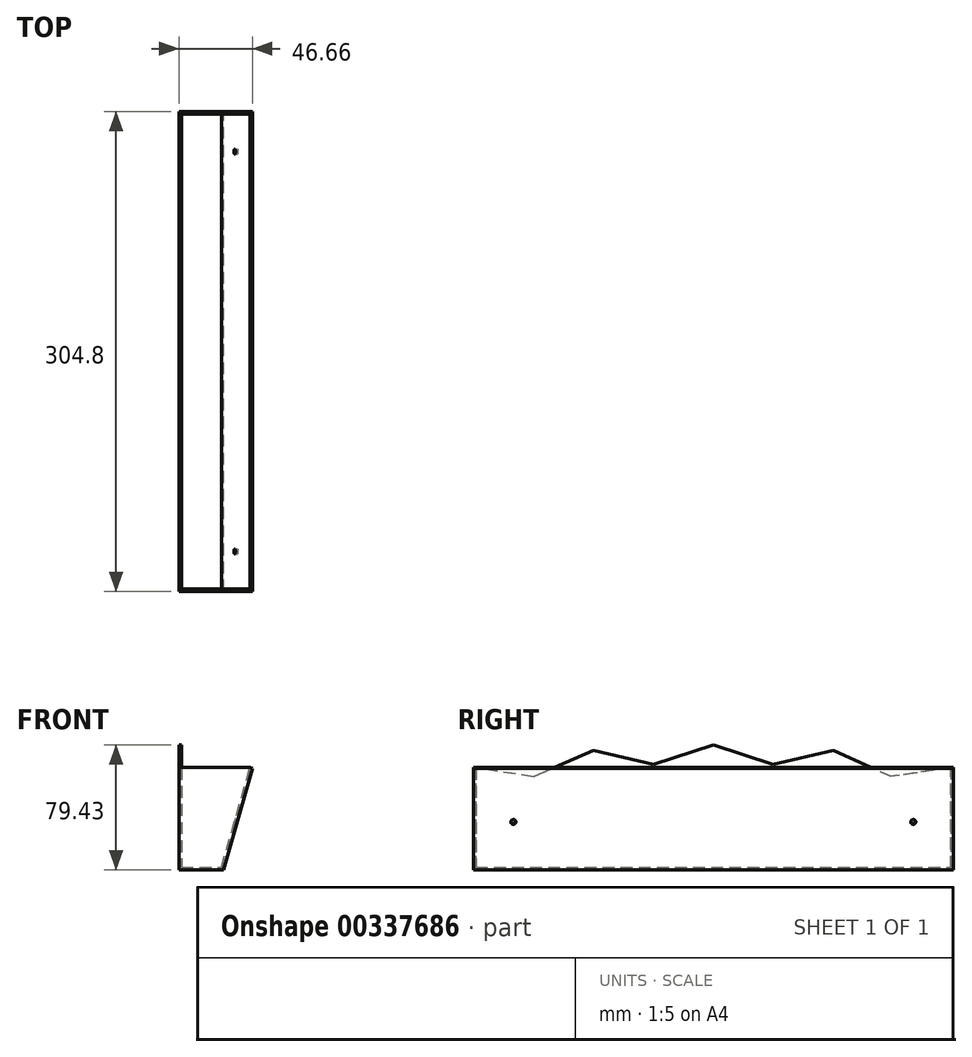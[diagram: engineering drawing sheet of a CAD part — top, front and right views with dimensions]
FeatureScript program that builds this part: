
annotation { "Feature Type Name" : "Feature", "Feature Type Description" : "" }
export const myFeature = defineFeature(function(context is Context, id is Id, definition is map)
    precondition{}
    {
        {
            var Q0;
            Q0=qCreatedBy(makeId("Front.planeOp"),FACE);
            var sketch = newSketch(context, id + "F0", { "sketchPlane" : qUnion([Q0])});
            skLineSegment(sketch, "E0", {"start": v(0, 63.5) * mm, "end": v(0, 0) * mm});
            skLineSegment(sketch, "E1", {"start": v(0, 0) * mm, "end": v(25.4, 0) * mm});
            skLineSegment(sketch, "E2", {"start": v(25.4, 0) * mm, "end": v(43.54, 63.5) * mm});
            skLineSegment(sketch, "E3", {"start": v(0, 63.5) * mm, "end": v(-1.59, 63.5) * mm});
            skLineSegment(sketch, "E4", {"start": v(-1.59, 63.5) * mm, "end": v(-1.59, -1.59) * mm});
            skLineSegment(sketch, "E5", {"start": v(-1.59, -1.59) * mm, "end": v(26.6, -1.59) * mm});
            skLineSegment(sketch, "E6", {"start": v(43.54, 63.5) * mm, "end": v(45.07, 63.06) * mm});
            skLineSegment(sketch, "E7", {"start": v(26.6, -1.59) * mm, "end": v(45.07, 63.06) * mm});
            skSolve(sketch);
        }
        {
            var Q0;
            Q0 = qSketchRegion(id + "F0", true);
            extrude(context, id + "F1", {"entities" : qUnion([Q0]), "depth" : 304.8 * mm});
        }
        {
            var Q0;
            Q0=makeQuery(id+"F1.opExtrude","SWEPT_FACE",FACE,{"disambiguationData":[OSD([sQuery(id+"F0.wireOp",EDGE,"E0")])]});
            var sketch = newSketch(context, id + "F2", { "sketchPlane" : qUnion([Q0])});
            skPoint(sketch, "E8", {"position": v(-0.14, 63.5) * mm});
            skPoint(sketch, "E9", {"position": v(-304.66, 63.5) * mm});
            skLineSegment(sketch, "E10", {"start": v(0, 50.6) * mm, "end": v(-304.8, 50.6) * mm});
            skArc(sketch, "E11", {"start": v(0, 50.6) * mm, "mid": v(-152.4, 66.42) * mm, "end": v(-304.8, 50.6) * mm});
            skLineSegment(sketch, "E12", {"start": v(-152.4, 50.6) * mm, "end": v(-152.4, 77.84) * mm});
            skPoint(sketch, "E12.startSnap0", {"position": v(-152.4, 63.5) * mm});
            skPoint(sketch, "E12.endSnap0", {"position": v(-152.4, 66.42) * mm});
            skLineSegment(sketch, "E13", {"start": v(-152.4, 63.5) * mm, "end": v(-76.2, 63.5) * mm});
            skLineSegment(sketch, "E14", {"start": v(-76.2, 63.5) * mm, "end": v(-76.2, 50.6) * mm});
            skLineSegment(sketch, "E15", {"start": v(-228.7, 63.5) * mm, "end": v(-228.7, 50.6) * mm});
            skLineSegment(sketch, "E16", {"start": v(0, 50.6) * mm, "end": v(-76.2, 50.6) * mm});
            skLineSegment(sketch, "E17", {"start": v(-304.8, 50.6) * mm, "end": v(-228.7, 50.6) * mm});
            skLineSegment(sketch, "E18", {"start": v(-76.2, 63.5) * mm, "end": v(-152.4, 63.5) * mm});
            skLineSegment(sketch, "E19", {"start": v(-0.14, 63.5) * mm, "end": v(-39.49, 57.78) * mm});
            skLineSegment(sketch, "E20", {"start": v(-39.49, 57.78) * mm, "end": v(-76.2, 74.28) * mm});
            skLineSegment(sketch, "E21", {"start": v(-76.2, 74.28) * mm, "end": v(-114.38, 65.44) * mm});
            skLineSegment(sketch, "E22", {"start": v(-114.38, 65.44) * mm, "end": v(-152.4, 77.84) * mm});
            skLineSegment(sketch, "E23", {"start": v(-152.4, 77.84) * mm, "end": v(-190.55, 65.43) * mm});
            skLineSegment(sketch, "E24", {"start": v(-190.55, 65.43) * mm, "end": v(-228.46, 74.28) * mm});
            skLineSegment(sketch, "E25", {"start": v(-228.7, 50.6) * mm, "end": v(-304.8, 50.6) * mm});
            skLineSegment(sketch, "E26", {"start": v(-266.75, 50.6) * mm, "end": v(-266.75, 57.56) * mm});
            skLineSegment(sketch, "E27", {"start": v(-228.46, 74.28) * mm, "end": v(-266.75, 57.56) * mm});
            skLineSegment(sketch, "E28", {"start": v(-266.75, 57.56) * mm, "end": v(-304.8, 63.5) * mm});
            skLineSegment(sketch, "E29.trimOffspring", {"start": v(-0.14, 63.5) * mm, "end": v(0, 63.5) * mm});
            skLineSegment(sketch, "E30", {"start": v(-39.49, 57.78) * mm, "end": v(-52.21, 63.5) * mm});
            skLineSegment(sketch, "E31", {"start": v(-39.49, 57.78) * mm, "end": v(0, 63.5) * mm});
            skSolve(sketch);
        }
        {
            var Q0;
            Q0=makeQuery(id+"F1.opExtrude","CAP_FACE",FACE,{"disambiguationData":[OSD([sQuery(id+"F0.wireOp",EDGE,"E0"),sQuery(id+"F0.wireOp",EDGE,"E1"),sQuery(id+"F0.wireOp",EDGE,"E2"),sQuery(id+"F0.wireOp",EDGE,"E3"),sQuery(id+"F0.wireOp",EDGE,"E4"),sQuery(id+"F0.wireOp",EDGE,"E5"),sQuery(id+"F0.wireOp",EDGE,"E6"),sQuery(id+"F0.wireOp",EDGE,"E7")])],"isStart":false});
            var sketch = newSketch(context, id + "F3", { "sketchPlane" : qUnion([Q0])});
            skLineSegment(sketch, "E32", {"start": v(-1.59, 63.5) * mm, "end": v(43.54, 63.5) * mm});
            skLineSegment(sketch, "E33", {"start": v(43.54, 63.5) * mm, "end": v(25.4, 0) * mm});
            skLineSegment(sketch, "E34", {"start": v(25.4, 0) * mm, "end": v(0, 0) * mm});
            skLineSegment(sketch, "E35", {"start": v(0, 0) * mm, "end": v(0, 63.5) * mm});
            skSolve(sketch);
        }
        {
            var Q0;
            Q0 = qSketchRegion(id + "F3", true);
            extrude(context, id + "F4", {"entities" : qUnion([Q0]), "operationType" : NewBodyOperationType.ADD, "oppositeDirection" : true, "depth" : 1.59 * mm});
        }
        {
            var Q0;
            Q0=makeQuery(id+"F1.opExtrude","CAP_FACE",FACE,{"disambiguationData":[OSD([sQuery(id+"F0.wireOp",EDGE,"E0"),sQuery(id+"F0.wireOp",EDGE,"E1"),sQuery(id+"F0.wireOp",EDGE,"E2"),sQuery(id+"F0.wireOp",EDGE,"E3"),sQuery(id+"F0.wireOp",EDGE,"E4"),sQuery(id+"F0.wireOp",EDGE,"E5"),sQuery(id+"F0.wireOp",EDGE,"E6"),sQuery(id+"F0.wireOp",EDGE,"E7")])],"isStart":true});
            var sketch = newSketch(context, id + "F5", { "sketchPlane" : qUnion([Q0])});
            skLineSegment(sketch, "E36", {"start": v(-43.54, 63.5) * mm, "end": v(0, 63.5) * mm});
            skLineSegment(sketch, "E37", {"start": v(0, 63.5) * mm, "end": v(0, 0) * mm});
            skLineSegment(sketch, "E38", {"start": v(0, 0) * mm, "end": v(-25.4, 0) * mm});
            skLineSegment(sketch, "E39", {"start": v(-25.4, 0) * mm, "end": v(-43.54, 63.5) * mm});
            skSolve(sketch);
        }
        {
            var Q0;
            Q0 = qSketchRegion(id + "F5", true);
            extrude(context, id + "F6", {"entities" : qUnion([Q0]), "operationType" : NewBodyOperationType.ADD, "oppositeDirection" : true, "depth" : 1.59 * mm});
        }
        {
            var Q0;
            Q0=makeQuery(id+"F1.opExtrude","SWEPT_FACE",FACE,{"disambiguationData":[OSD([sQuery(id+"F0.wireOp",EDGE,"E7")])]});
            var sketch = newSketch(context, id + "F7", { "sketchPlane" : qUnion([Q0])});
            skCircle(sketch, "E40", {"center": v(-279.4, 37.53) * mm, "radius": 1.59 * mm});
            skCircle(sketch, "E41", {"center": v(-25.4, 37.53) * mm, "radius": 1.59 * mm});
            skLineSegment(sketch, "E42.bottom", {"start": v(-280.99, 37.53) * mm, "end": v(-304.8, 37.53) * mm});
            skLineSegment(sketch, "E42.top", {"start": v(-279.4, 5.78) * mm, "end": v(-304.8, 5.78) * mm});
            skLineSegment(sketch, "E42.left", {"start": v(-279.4, 35.94) * mm, "end": v(-279.4, 5.78) * mm});
            skLineSegment(sketch, "E42.right", {"start": v(-304.8, 37.53) * mm, "end": v(-304.8, 5.78) * mm});
            skLineSegment(sketch, "E43.bottom", {"start": v(-23.81, 37.53) * mm, "end": v(0, 37.53) * mm});
            skLineSegment(sketch, "E43.top", {"start": v(-25.4, 5.78) * mm, "end": v(0, 5.78) * mm});
            skLineSegment(sketch, "E43.left", {"start": v(-25.4, 35.94) * mm, "end": v(-25.4, 5.78) * mm});
            skLineSegment(sketch, "E43.right", {"start": v(0, 37.53) * mm, "end": v(0, 5.78) * mm});
            skSolve(sketch);
        }
        {
            var Q0;
            {var subQ0=sQuery(id+"F7.wireOp",EDGE,"E40");var subQ1=makeQuery(id+"F7.imprint","INTERSECT",VERTEX,{"derivedFrom":[subQ0,sQuery(id+"F7.wireOp",EDGE,"E42.bottom")]});Q0=makeQuery(id+"F7.imprint","IMPRINT",FACE,{"disambiguationData":[TD([[makeQuery(id+"F7.imprint","IMPRINT",EDGE,{"disambiguationData":[TD([[subQ1,-1.0]])],"derivedFrom":subQ0}),1.0]])]});}
            var Q1;
            {var subQ0=sQuery(id+"F7.wireOp",EDGE,"E41");var subQ1=makeQuery(id+"F7.imprint","INTERSECT",VERTEX,{"derivedFrom":[subQ0,sQuery(id+"F7.wireOp",EDGE,"E43.bottom")]});Q1=makeQuery(id+"F7.imprint","IMPRINT",FACE,{"disambiguationData":[TD([[makeQuery(id+"F7.imprint","IMPRINT",EDGE,{"disambiguationData":[TD([[subQ1,-1.0]])],"derivedFrom":subQ0}),1.0]])]});}
            var Q2;
            Q2=sQuery(id+"F7.wireOp",EDGE,"E40");
            var Q3;
            Q3=sQuery(id+"F7.wireOp",EDGE,"E41");
            extrude(context, id + "F8", {"entities" : qUnion([Q0, Q1]), "operationType" : NewBodyOperationType.REMOVE, "surfaceEntities" : qUnion([Q2, Q3]), "oppositeDirection" : true, "depth" : 25.4 * mm});
        }
        {
            var Q0;
            {var subQ0=sQuery(id+"F2.wireOp",EDGE,"E19");Q0=makeQuery(id+"F2.imprint","IMPRINT",FACE,{"disambiguationData":[TD([[makeQuery(id+"F2.imprint","IMPRINT",EDGE,{"derivedFrom":subQ0}),-1.0]])]});}
            var Q1;
            {var subQ0=sQuery(id+"F2.wireOp",EDGE,"E28");Q1=makeQuery(id+"F2.imprint","IMPRINT",FACE,{"disambiguationData":[TD([[makeQuery(id+"F2.imprint","IMPRINT",EDGE,{"derivedFrom":subQ0}),-1.0]])]});}
            extrude(context, id + "F9", {"entities" : qUnion([Q0, Q1]), "operationType" : NewBodyOperationType.REMOVE, "oppositeDirection" : true, "depth" : 25.4 * mm});
        }
        {
            var Q0;
            Q0 = qSketchRegion(id + "F2", true);
            extrude(context, id + "F10", {"entities" : qUnion([Q0]), "operationType" : NewBodyOperationType.ADD, "oppositeDirection" : true, "depth" : 1.59 * mm});
        }
    });
